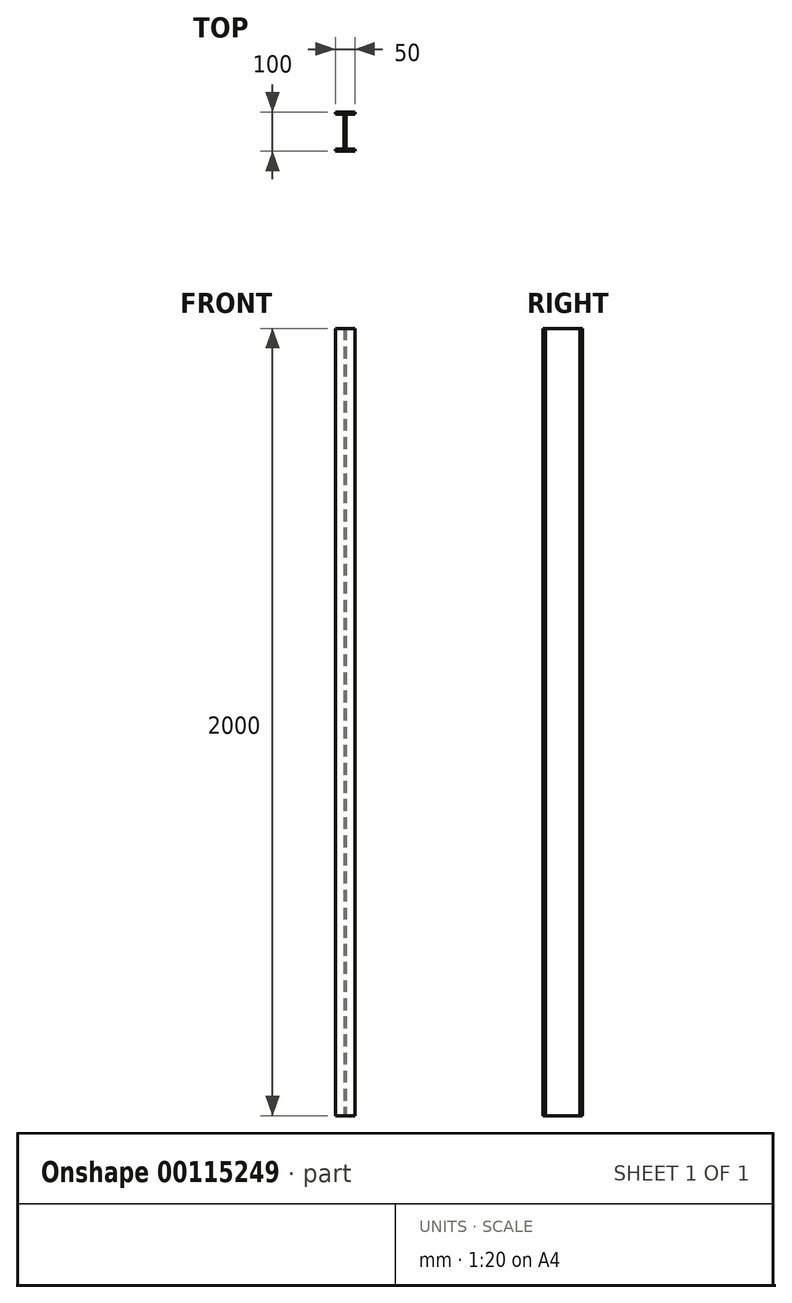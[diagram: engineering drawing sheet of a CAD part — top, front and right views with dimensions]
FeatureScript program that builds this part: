
annotation { "Feature Type Name" : "Feature", "Feature Type Description" : "" }
export const myFeature = defineFeature(function(context is Context, id is Id, definition is map)
    precondition{}
    {
        {
            var Q0;
            Q0=qCreatedBy(makeId("Top.planeOp"),FACE);
            var sketch = newSketch(context, id + "F0", { "sketchPlane" : qUnion([Q0])});
            skLineSegment(sketch, "E0.bottom", {"start": v(0, 0) * mm, "end": v(-50, 0) * mm});
            skLineSegment(sketch, "E0.top", {"start": v(0, -100) * mm, "end": v(-50, -100) * mm});
            skLineSegment(sketch, "E0.left", {"start": v(0, 0) * mm, "end": v(0, -6) * mm});
            skLineSegment(sketch, "E0.right", {"start": v(-50, 0) * mm, "end": v(-50, -6) * mm});
            skLineSegment(sketch, "E1.bottom", {"start": v(-50, -6) * mm, "end": v(-27.5, -6) * mm});
            skLineSegment(sketch, "E1.top", {"start": v(-50, -94) * mm, "end": v(-27.5, -94) * mm});
            skLineSegment(sketch, "E1.right", {"start": v(-27.5, -6) * mm, "end": v(-27.5, -94) * mm});
            skLineSegment(sketch, "E2.bottom", {"start": v(0, -6) * mm, "end": v(-22.5, -6) * mm});
            skLineSegment(sketch, "E2.top", {"start": v(0, -94) * mm, "end": v(-22.5, -94) * mm});
            skLineSegment(sketch, "E2.right", {"start": v(-22.5, -6) * mm, "end": v(-22.5, -94) * mm});
            skPoint(sketch, "E3.orphan", {"position": v(-25, 0) * mm});
            skPoint(sketch, "E4.orphan", {"position": v(-25, -100) * mm});
            skLineSegment(sketch, "E5.trimOffspring", {"start": v(-50, -94) * mm, "end": v(-50, -100) * mm});
            skLineSegment(sketch, "E6.trimOffspring", {"start": v(0, -94) * mm, "end": v(0, -100) * mm});
            skLineSegment(sketch, "E7", {"start": v(-25, 0) * mm, "end": v(-25, -100) * mm, "construction": true});
            skSolve(sketch);
        }
        {
            var Q0;
            Q0=makeQuery(id+"F0.imprint","IMPRINT",FACE,{"disambiguationData":[TD([[makeQuery(id+"F0.imprint","IMPRINT",EDGE,{"derivedFrom":sQuery(id+"F0.wireOp",EDGE,"E0.bottom")}),1.0]])]});
            extrude(context, id + "F1", {"entities" : qUnion([Q0]), "depth" : 2000 * mm});
        }
    });
